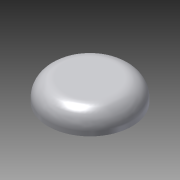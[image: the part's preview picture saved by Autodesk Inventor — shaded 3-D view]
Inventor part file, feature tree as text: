
AUTODESK INVENTOR PART (.ipt)
format: ipt  version: 2015 (Build 190159000, 159)  size: 102,400 bytes
history: native  units: in
note: dims shown in document units (in); Inventor stores cm internally (conversion verified against a paired STEP export)
features: extrude x1, fillet x1, sketch x1
ambient origin geometry x8: Origin, YZ Plane, XZ Plane, XY Plane, X Axis, Y Axis, Z Axis, Center Point
bodies: Solid1 (feature_tree)
feature tree (3):
  extrude  "Extrusion1"  Depth=0.125in TaperAngle=0.0deg
  fillet  "Fillet1"  Radius=0.1in
  sketch  "Sketch1"  dims[d0=0.5in d1=0.125in d2=0.0in d3=0.1in]
